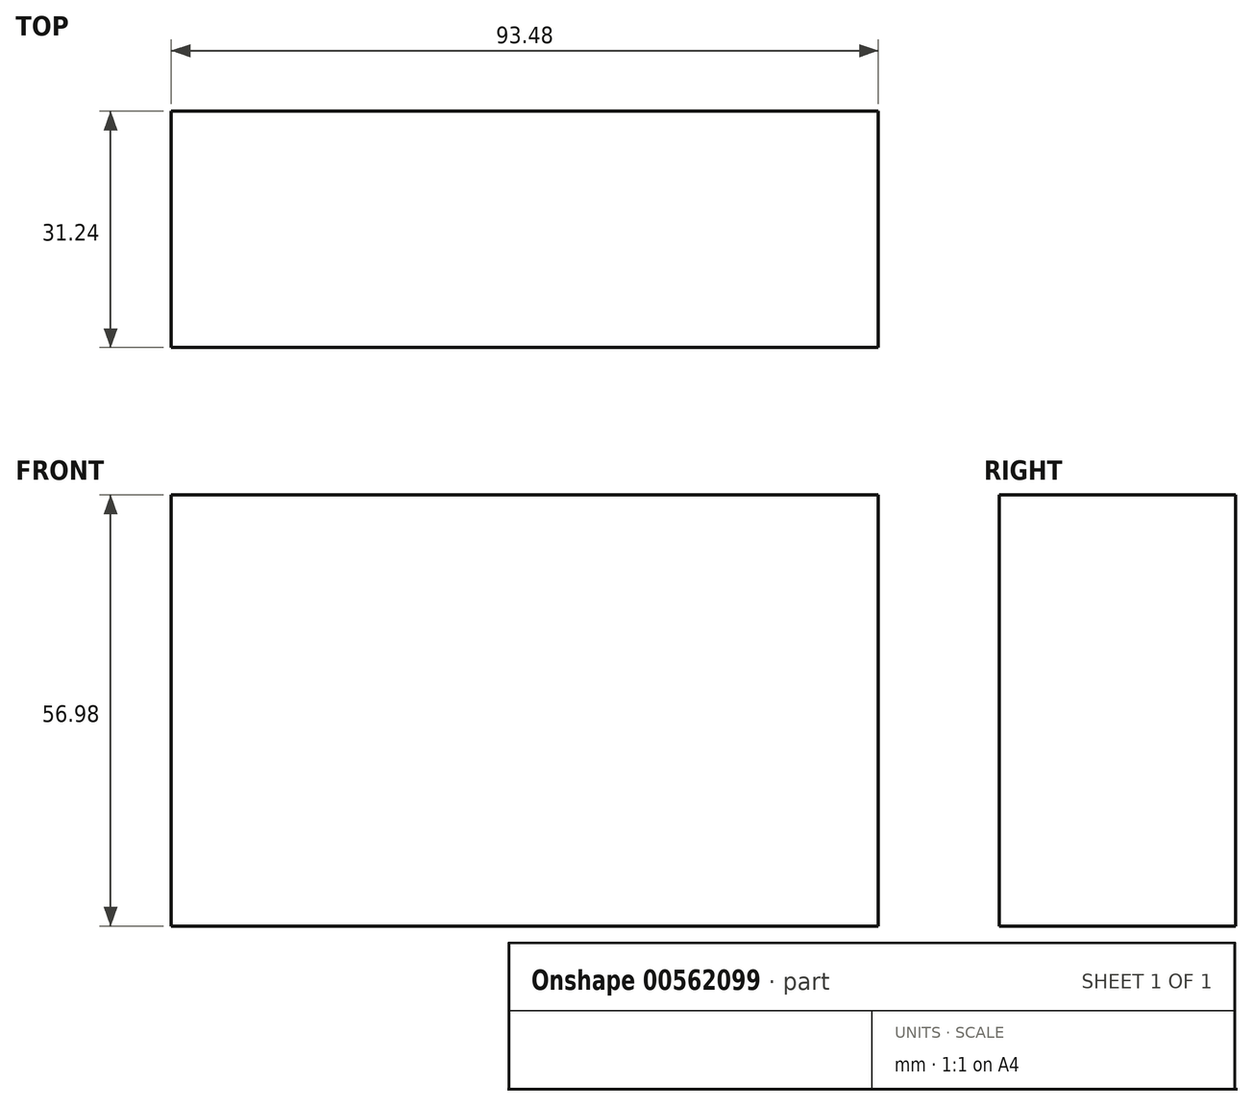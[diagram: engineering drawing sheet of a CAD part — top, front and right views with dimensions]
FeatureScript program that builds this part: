
annotation { "Feature Type Name" : "Feature", "Feature Type Description" : "" }
export const myFeature = defineFeature(function(context is Context, id is Id, definition is map)
    precondition{}
    {
        {
            var Q0;
            Q0=qCreatedBy(makeId("Front.planeOp"),FACE);
            var sketch = newSketch(context, id + "F0", { "sketchPlane" : qUnion([Q0])});
            skLineSegment(sketch, "E0.bottom", {"start": v(46.74, 28.5) * mm, "end": v(-46.74, 28.5) * mm});
            skLineSegment(sketch, "E0.top", {"start": v(46.74, -28.5) * mm, "end": v(-46.74, -28.5) * mm});
            skLineSegment(sketch, "E0.left", {"start": v(46.74, 28.5) * mm, "end": v(46.74, -28.5) * mm});
            skLineSegment(sketch, "E0.right", {"start": v(-46.74, 28.5) * mm, "end": v(-46.74, -28.5) * mm});
            skPoint(sketch, "E0.middle", {"position": v(0, 0) * mm});
            skSolve(sketch);
        }
        {
            var Q0;
            Q0=makeQuery(id+"F0.imprint","IMPRINT",FACE,{"disambiguationData":[TD([[makeQuery(id+"F0.imprint","IMPRINT",EDGE,{"derivedFrom":sQuery(id+"F0.wireOp",EDGE,"E0.bottom")}),1.0]])]});
            extrude(context, id + "F1", {"entities" : qUnion([Q0]), "depth" : 31.24 * mm, "offsetDistance" : 25.4 * mm});
        }
    });
